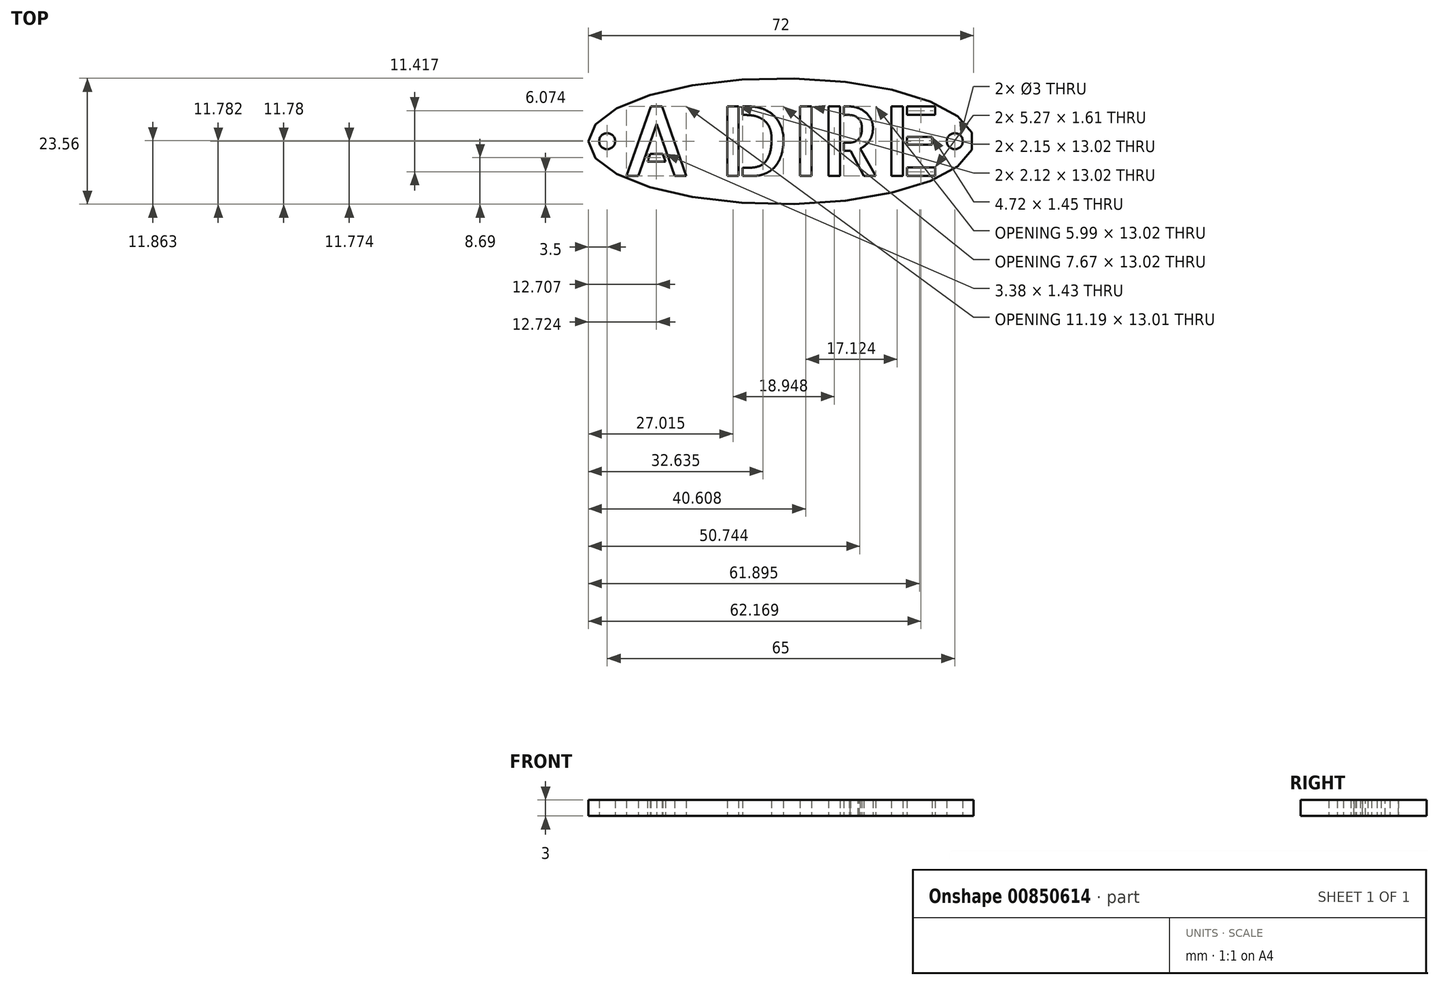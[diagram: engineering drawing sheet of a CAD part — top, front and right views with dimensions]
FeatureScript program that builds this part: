
annotation { "Feature Type Name" : "Feature", "Feature Type Description" : "" }
export const myFeature = defineFeature(function(context is Context, id is Id, definition is map)
    precondition{}
    {
        {
            var Q0;
            Q0=qCreatedBy(makeId("Top.planeOp"),FACE);
            var sketch = newSketch(context, id + "F0", { "sketchPlane" : qUnion([Q0])});
            skText(sketch, "E0", { "text": "A DIRE", "fontName": "AllertaStencil-Regular.ttf"});
            skLineSegment(sketch, "E1", {"start": v(30, 0) * mm, "end": v(-30, 0) * mm, "construction": true});
            skEllipse(sketch, "E2", {"center": v(0, 0) * mm, "majorRadius": 36 * mm, "minorRadius": 11.78 * mm, "majorAxis": v(-1, 0)});
            skCircle(sketch, "E3", {"center": v(-32.5, 0) * mm, "radius": 1.5 * mm});
            skCircle(sketch, "E4", {"center": v(32.5, 0) * mm, "radius": 1.5 * mm});
            const initialGuessF0  = {"E0": [-0.03, -0.00651, 1, 0, 0.01303]};
            skSetInitialGuess(sketch, initialGuessF0);
            skSolve(sketch);
        }
        {
            var Q0;
            Q0=makeQuery(id+"F0.imprint","IMPRINT",FACE,{"disambiguationData":[TD([[makeQuery(id+"F0.imprint","IMPRINT",EDGE,{"derivedFrom":sQuery(id+"F0.wireOp",EDGE,"E0.sketch_text.stroke-0")}),1.0]])]});
            extrude(context, id + "F1", {"entities" : qUnion([Q0]), "depth" : 3 * mm, "offsetDistance" : 25 * mm});
        }
    });
